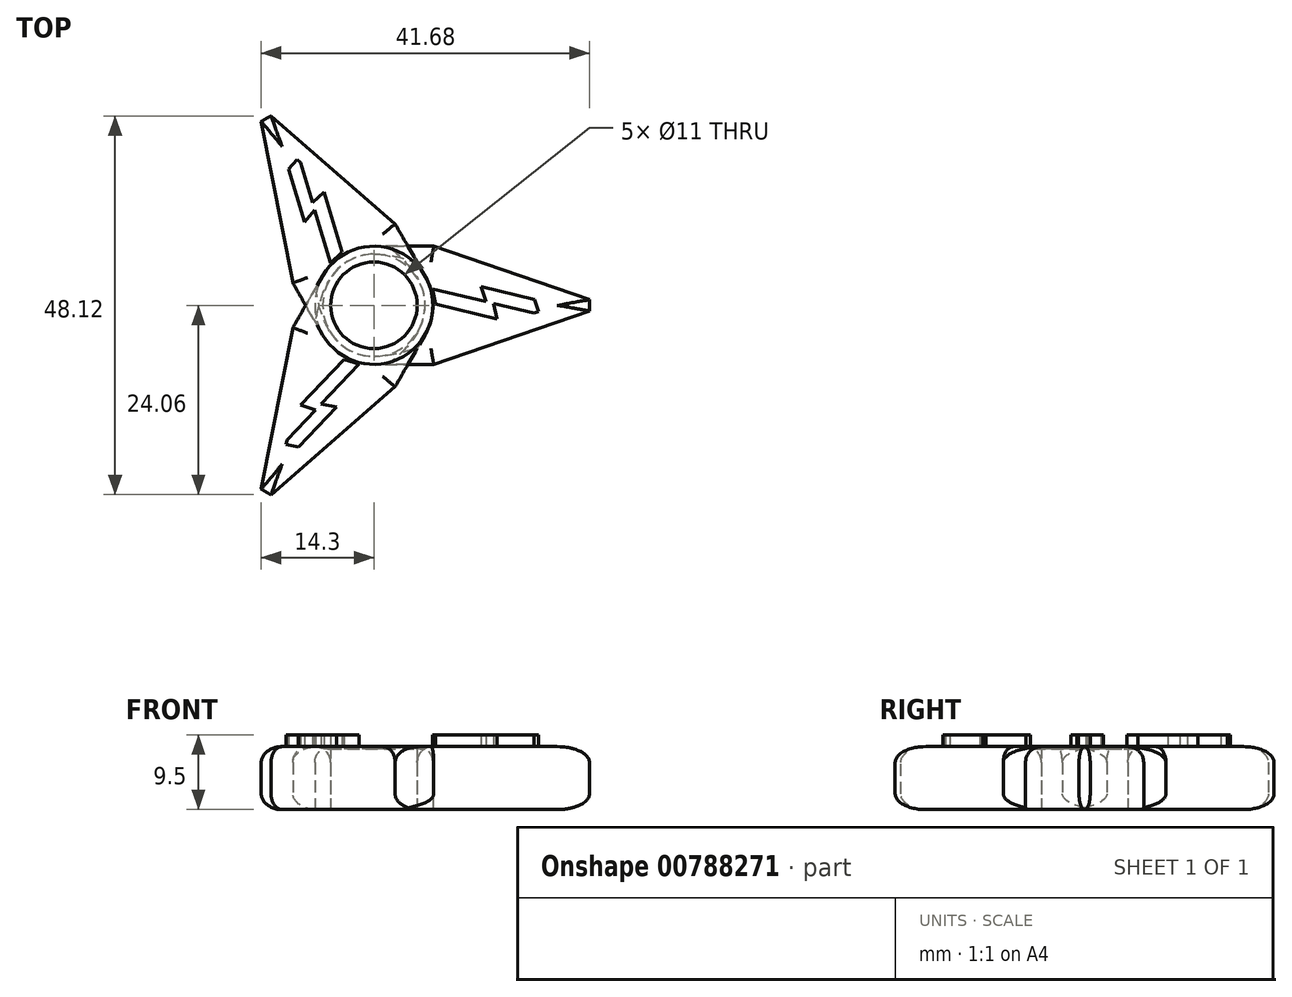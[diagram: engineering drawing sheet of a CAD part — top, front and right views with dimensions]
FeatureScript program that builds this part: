
annotation { "Feature Type Name" : "Feature", "Feature Type Description" : "" }
export const myFeature = defineFeature(function(context is Context, id is Id, definition is map)
    precondition{}
    {
        {
            var Q0;
            Q0=qCreatedBy(makeId("Top.planeOp"),FACE);
            var sketch = newSketch(context, id + "F0", { "sketchPlane" : qUnion([Q0])});
            skCircle(sketch, "E0", {"center": v(0, 0) * mm, "radius": 5.5 * mm});
            skCircle(sketch, "E1", {"center": v(0, 0) * mm, "radius": 7.5 * mm});
            skArc(sketch, "E2", {"start": v(1.87, 7.26) * mm, "mid": v(1.4, 6.35) * mm, "end": v(1, 5.4) * mm});
            skPoint(sketch, "E3.end.orphan", {"position": v(68.12, 0) * mm});
            skPoint(sketch, "E4.orphan", {"position": v(15, -15) * mm});
            skPoint(sketch, "E5.orphan", {"position": v(11.12, 14.5) * mm});
            skArc(sketch, "E6", {"start": v(13.8, 5.37) * mm, "mid": v(9.5, 0) * mm, "end": v(13.8, -5.37) * mm});
            skArc(sketch, "E7.trimOffspring", {"start": v(7.6, 13.05) * mm, "mid": v(7.49, 12.98) * mm, "end": v(7.38, 12.92) * mm});
            skPoint(sketch, "E8.end.orphan", {"position": v(69.04, 0) * mm});
            skPoint(sketch, "E9.start.orphan", {"position": v(13.6, 15) * mm});
            skPoint(sketch, "E10.start.orphan", {"position": v(0, -7.5) * mm});
            skPoint(sketch, "E11.start.orphan", {"position": v(9.16, 11) * mm});
            skPoint(sketch, "E12.start.orphan", {"position": v(0, 7.5) * mm});
            skArc(sketch, "E13", {"start": v(10.99, 6.34) * mm, "mid": v(7.5, 0) * mm, "end": v(10.99, -6.34) * mm});
            skPoint(sketch, "E14.orphan", {"position": v(13.6, 10.91) * mm});
            skPoint(sketch, "E15.orphan", {"position": v(7.5, -11.25) * mm});
            skPoint(sketch, "E16.orphan", {"position": v(5.56, 11) * mm});
            skLineSegment(sketch, "E17", {"start": v(0, 7.5) * mm, "end": v(7.6, 7.5) * mm});
            skLineSegment(sketch, "E18", {"start": v(15, 4.96) * mm, "end": v(15, -4.96) * mm});
            skLineSegment(sketch, "E19", {"start": v(7.6, -7.5) * mm, "end": v(0, -7.5) * mm});
            skLineSegment(sketch, "E20", {"start": v(0, 7.5) * mm, "end": v(0, -7.5) * mm});
            skLineSegment(sketch, "E21", {"start": v(7.6, 7.5) * mm, "end": v(29.44, 0) * mm});
            skLineSegment(sketch, "E22", {"start": v(29.44, 0) * mm, "end": v(7.6, -7.5) * mm});
            skArc(sketch, "E23.trimOffspring", {"start": v(22.06, -2.54) * mm, "mid": v(22.5, 0) * mm, "end": v(22.06, 2.54) * mm});
            skArc(sketch, "E24.trimOffspring", {"start": v(19.24, -3.5) * mm, "mid": v(20.5, 0) * mm, "end": v(19.24, 3.5) * mm});
            skSolve(sketch);
        }
        {
            var Q0;
            Q0=makeQuery(id+"F0.imprint","IMPRINT",FACE,{"disambiguationData":[TD([[makeQuery(id+"F0.imprint","IMPRINT",EDGE,{"derivedFrom":sQuery(id+"F0.wireOp",EDGE,"E0")}),-1.0]])]});
            var Q1;
            {var subQ7=sQuery(id+"F0.wireOp",EDGE,"E6");var subQ12=makeQuery(id+"F0.imprint","IMPRINT",VERTEX,{"disambiguationData":[OD(0.0)],"derivedFrom":subQ7});Q1=makeQuery(id+"F0.imprint","IMPRINT",FACE,{"disambiguationData":[TD([[makeQuery(id+"F0.imprint","IMPRINT",EDGE,{"disambiguationData":[TD([[subQ12,1.0]])],"derivedFrom":subQ7}),-1.0]])]});}
            var Q2;
            {var subQ0=sQuery(id+"F0.wireOp",EDGE,"E6");var subQ4=makeQuery(id+"F0.imprint","IMPRINT",VERTEX,{"disambiguationData":[OD(0.0)],"derivedFrom":subQ0});Q2=makeQuery(id+"F0.imprint","IMPRINT",FACE,{"disambiguationData":[TD([[makeQuery(id+"F0.imprint","IMPRINT",EDGE,{"disambiguationData":[TD([[subQ4,1.0]])],"derivedFrom":subQ0}),1.0]])]});}
            var Q3;
            {var subQ0=sQuery(id+"F0.wireOp",EDGE,"E19");Q3=makeQuery(id+"F0.imprint","IMPRINT",FACE,{"disambiguationData":[TD([[makeQuery(id+"F0.imprint","IMPRINT",EDGE,{"derivedFrom":subQ0}),-1.0]])]});}
            var Q4;
            {var subQ0=sQuery(id+"F0.wireOp",EDGE,"E17");Q4=makeQuery(id+"F0.imprint","IMPRINT",FACE,{"disambiguationData":[TD([[makeQuery(id+"F0.imprint","IMPRINT",EDGE,{"derivedFrom":subQ0}),-1.0]])]});}
            var Q5;
            {var subQ4=sQuery(id+"F0.wireOp",EDGE,"E2");Q5=makeQuery(id+"F0.imprint","IMPRINT",FACE,{"disambiguationData":[TD([[makeQuery(id+"F0.imprint","IMPRINT",EDGE,{"derivedFrom":subQ4}),1.0]])]});}
            var Q6;
            {var subQ0=sQuery(id+"F0.wireOp",EDGE,"E18");Q6=makeQuery(id+"F0.imprint","IMPRINT",FACE,{"disambiguationData":[TD([[makeQuery(id+"F0.imprint","IMPRINT",EDGE,{"derivedFrom":subQ0}),1.0]])]});}
            var Q7;
            {var subQ0=sQuery(id+"F0.wireOp",EDGE,"E23.trimOffspring");Q7=makeQuery(id+"F0.imprint","IMPRINT",FACE,{"disambiguationData":[TD([[makeQuery(id+"F0.imprint","IMPRINT",EDGE,{"derivedFrom":subQ0}),1.0]])]});}
            var Q8;
            {var subQ3=sQuery(id+"F0.wireOp",EDGE,"E23.trimOffspring");Q8=makeQuery(id+"F0.imprint","IMPRINT",FACE,{"disambiguationData":[TD([[makeQuery(id+"F0.imprint","IMPRINT",EDGE,{"derivedFrom":subQ3}),-1.0]])]});}
            extrude(context, id + "F1", {"entities" : qUnion([Q0, Q1, Q2, Q3, Q4, Q5, Q6, Q7, Q8]), "depth" : 8 * mm, "offsetDistance" : 25 * mm});
        }
        {
            var Q0;
            Q0=qCreatedBy(makeId("Right.planeOp"),FACE);
            var sketch = newSketch(context, id + "F2", { "sketchPlane" : qUnion([Q0])});
            skLineSegment(sketch, "E25", {"start": v(0, 0) * mm, "end": v(0, 45.5) * mm});
            skSolve(sketch);
        }
        {
            var Q0;
            Q0=makeQuery(id+"F1.opExtrude","SWEPT_BODY",BODY,{"disambiguationData":[OSD([sQuery(id+"F0.wireOp",EDGE,"E0"),sQuery(id+"F0.wireOp",EDGE,"E1"),sQuery(id+"F0.wireOp",EDGE,"c1pOTcFN-srbn-hujo-DCLo-aXCk1lQ58b2f"),sQuery(id+"F0.wireOp",EDGE,"E2"),sQuery(id+"F0.wireOp",EDGE,"E10"),sQuery(id+"F0.wireOp",EDGE,"E12")])]});
            var Q1;
            Q1=sQuery(id+"F2.wireOp",EDGE,"E25");
            circularPattern(context, id + "F3", {"entities" : qUnion([Q0]), "axis" : qUnion([Q1]), "angle" : 360 * degree, "instanceCount" : 3, "equalSpace" : true});
        }
        {
            var Q0;
            Q0=makeQuery(id+"F1.opExtrude","CAP_EDGE",EDGE,{"disambiguationData":[OSD([sQuery(id+"F0.wireOp",EDGE,"E22")])],"isStart":false});
            var Q1;
            Q1=makeQuery(id+"F1.opExtrude","CAP_FACE",FACE,{"disambiguationData":[OSD([sQuery(id+"F0.wireOp",EDGE,"E0"),sQuery(id+"F0.wireOp",EDGE,"E1"),sQuery(id+"F0.wireOp",EDGE,"E17"),sQuery(id+"F0.wireOp",EDGE,"E19"),sQuery(id+"F0.wireOp",EDGE,"E21"),sQuery(id+"F0.wireOp",EDGE,"E22")])],"isStart":false});
            var Q2;
            Q2=makeQuery(id+"F1.opExtrude","CAP_EDGE",EDGE,{"disambiguationData":[OSD([sQuery(id+"F0.wireOp",EDGE,"E22")])],"isStart":true});
            var Q3;
            Q3=makeQuery(id+"F1.opExtrude","CAP_EDGE",EDGE,{"disambiguationData":[OSD([sQuery(id+"F0.wireOp",EDGE,"E21")])],"isStart":true});
            var Q4;
            Q4=makeQuery(id+"F3.opPattern","COPY",EDGE,{"derivedFrom":makeQuery(id+"F1.opExtrude","CAP_EDGE",EDGE,{"disambiguationData":[OSD([sQuery(id+"F0.wireOp",EDGE,"E22")])],"isStart":true}),"instanceName":"1"});
            var Q5;
            Q5=makeQuery(id+"F3.opPattern","COPY",EDGE,{"derivedFrom":makeQuery(id+"F1.opExtrude","CAP_EDGE",EDGE,{"disambiguationData":[OSD([sQuery(id+"F0.wireOp",EDGE,"E21")])],"isStart":true}),"instanceName":"1"});
            var Q6;
            Q6=makeQuery(id+"F3.opPattern","COPY",EDGE,{"derivedFrom":makeQuery(id+"F1.opExtrude","CAP_EDGE",EDGE,{"disambiguationData":[OSD([sQuery(id+"F0.wireOp",EDGE,"E22")])],"isStart":false}),"instanceName":"1"});
            var Q7;
            Q7=makeQuery(id+"F3.opPattern","COPY",EDGE,{"derivedFrom":makeQuery(id+"F1.opExtrude","CAP_EDGE",EDGE,{"disambiguationData":[OSD([sQuery(id+"F0.wireOp",EDGE,"E21")])],"isStart":false}),"instanceName":"1"});
            var Q8;
            Q8=makeQuery(id+"F3.opPattern","COPY",EDGE,{"derivedFrom":makeQuery(id+"F1.opExtrude","CAP_EDGE",EDGE,{"disambiguationData":[OSD([sQuery(id+"F0.wireOp",EDGE,"E22")])],"isStart":false}),"instanceName":"2"});
            var Q9;
            Q9=makeQuery(id+"F3.opPattern","COPY",EDGE,{"derivedFrom":makeQuery(id+"F1.opExtrude","CAP_EDGE",EDGE,{"disambiguationData":[OSD([sQuery(id+"F0.wireOp",EDGE,"E22")])],"isStart":true}),"instanceName":"2"});
            var Q10;
            Q10=makeQuery(id+"F3.opPattern","COPY",EDGE,{"derivedFrom":makeQuery(id+"F1.opExtrude","CAP_EDGE",EDGE,{"disambiguationData":[OSD([sQuery(id+"F0.wireOp",EDGE,"E21")])],"isStart":true}),"instanceName":"2"});
            var Q11;
            Q11=makeQuery(id+"F3.opPattern","COPY",EDGE,{"derivedFrom":makeQuery(id+"F1.opExtrude","CAP_EDGE",EDGE,{"disambiguationData":[OSD([sQuery(id+"F0.wireOp",EDGE,"E21")])],"isStart":false}),"instanceName":"2"});
            fillet(context, id + "F4", {"entities" : qUnion([Q0, Q1, Q2, Q3, Q4, Q5, Q6, Q7, Q8, Q9, Q10, Q11]), "radius" : 2 * mm, "tangentPropagation" : true, "allowEdgeOverflow" : false});
        }
        {
            var Q0;
            Q0=makeQuery(id+"F1.opExtrude","SWEPT_EDGE",EDGE,{"disambiguationData":[OSD([sQuery(id+"F0.wireOp",EDGE,"E21"),sQuery(id+"F0.wireOp",EDGE,"E22")])]});
            var Q1;
            Q1=makeQuery(id+"F3.opPattern","COPY",EDGE,{"derivedFrom":makeQuery(id+"F1.opExtrude","SWEPT_EDGE",EDGE,{"disambiguationData":[OSD([sQuery(id+"F0.wireOp",EDGE,"E21"),sQuery(id+"F0.wireOp",EDGE,"E22")])]}),"instanceName":"2"});
            var Q2;
            Q2=makeQuery(id+"F3.opPattern","COPY",EDGE,{"derivedFrom":makeQuery(id+"F1.opExtrude","SWEPT_EDGE",EDGE,{"disambiguationData":[OSD([sQuery(id+"F0.wireOp",EDGE,"E21"),sQuery(id+"F0.wireOp",EDGE,"E22")])]}),"instanceName":"1"});
            chamfer(context, id + "F5", {"entities" : qUnion([Q0, Q1, Q2]), "width" : .75 * mm, "tangentPropagation" : true});
        }
        {
            var Q0;
            Q0=makeQuery(id+"F1.opExtrude","CAP_FACE",FACE,{"disambiguationData":[OSD([sQuery(id+"F0.wireOp",EDGE,"E0"),sQuery(id+"F0.wireOp",EDGE,"E1"),sQuery(id+"F0.wireOp",EDGE,"E10"),sQuery(id+"F0.wireOp",EDGE,"E12"),sQuery(id+"F0.wireOp",EDGE,"nMp6aDYQ-EUBn-gi7Y-1vA0-NtzO73nNKpQa"),sQuery(id+"F0.wireOp",EDGE,"ucYtV5Ov-8Bkq-GZmE-3TVC-n8T25JyWtEvq"),sQuery(id+"F0.wireOp",EDGE,"E11"),sQuery(id+"F0.wireOp",EDGE,"I5XwJxgH-NOVb-tVkx-Tq6v-A4jt36yrtx08"),sQuery(id+"F0.wireOp",EDGE,"dG7KTNho-NzEc-45em-pvrw-m2yzHunjuOYy"),sQuery(id+"F0.wireOp",EDGE,"ejjroDpW-kohF-Plgn-IGdK-DfK92TdWfwf9"),sQuery(id+"F0.wireOp",EDGE,"NdLykpWK-kagu-JWG3-DeJg-S52FodjAq7Sg"),sQuery(id+"F0.wireOp",EDGE,"0NwxsXWG-HWzj-xsas-FfyO-PVFYgCGhCiFI")])],"isStart":false});
            var sketch = newSketch(context, id + "F6", { "sketchPlane" : qUnion([Q0])});
            skPoint(sketch, "E26.end.orphan", {"position": v(20.02, 0) * mm});
            skPoint(sketch, "E27.orphan", {"position": v(27.12, -4.48) * mm});
            skPoint(sketch, "E28.end.orphan", {"position": v(43.2, 0) * mm});
            skPoint(sketch, "E29.end.orphan", {"position": v(27.12, -1.7) * mm});
            skLineSegment(sketch, "E30", {"start": v(7.42, 2.1) * mm, "end": v(7.86, 0.14) * mm});
            skLineSegment(sketch, "E31", {"start": v(7.86, 0.14) * mm, "end": v(15.64, -1.72) * mm});
            skLineSegment(sketch, "E32", {"start": v(15.64, -1.72) * mm, "end": v(15.2, 0.23) * mm});
            skLineSegment(sketch, "E33", {"start": v(14.23, 0.46) * mm, "end": v(7.42, 2.1) * mm});
            skLineSegment(sketch, "E34", {"start": v(15.2, 0.23) * mm, "end": v(21.03, -1.16) * mm});
            skLineSegment(sketch, "E35", {"start": v(21.03, -1.16) * mm, "end": v(20.4, 0.73) * mm});
            skLineSegment(sketch, "E36", {"start": v(20.4, 0.73) * mm, "end": v(13.58, 2.36) * mm});
            skLineSegment(sketch, "E37", {"start": v(13.58, 2.36) * mm, "end": v(14.23, 0.46) * mm});
            skPoint(sketch, "E38.end.orphan", {"position": v(8.56, -2.53) * mm});
            skPoint(sketch, "E39.orphan", {"position": v(15.66, -7) * mm});
            skPoint(sketch, "E40.end.orphan", {"position": v(31.75, -2.53) * mm});
            skPoint(sketch, "E41.end.orphan", {"position": v(15.66, -4.22) * mm});
            skSolve(sketch);
        }
        {
            var Q0;
            Q0=makeQuery(id+"F6.imprint","IMPRINT",FACE,{"disambiguationData":[TD([[makeQuery(id+"F6.imprint","IMPRINT",EDGE,{"derivedFrom":sQuery(id+"F6.wireOp",EDGE,"E26")}),1.0]])]});
            var Q1;
            {var subQ6=sQuery(id+"F6.wireOp",EDGE,"df851d8e-270d-4600-adc7-b6d222d9d4d0");Q1=makeQuery(id+"F6.imprint","IMPRINT",FACE,{"disambiguationData":[TD([[makeQuery(id+"F6.imprint","IMPRINT",EDGE,{"derivedFrom":subQ6}),1.0]])]});}
            var Q2;
            Q2=makeQuery(id+"F6.imprint","IMPRINT",FACE,{"disambiguationData":[TD([[makeQuery(id+"F6.imprint","IMPRINT",EDGE,{"derivedFrom":sQuery(id+"F6.wireOp",EDGE,"E30")}),1.0]])]});
            extrude(context, id + "F7", {"entities" : qUnion([Q0, Q1, Q2]), "operationType" : NewBodyOperationType.ADD, "depth" : 1.5 * mm, "offsetDistance" : 25 * mm});
        }
        {
            var Q0;
            Q0=makeQuery(id+"F1.opExtrude","SWEPT_BODY",BODY,{"disambiguationData":[OSD([sQuery(id+"F0.wireOp",EDGE,"E0"),sQuery(id+"F0.wireOp",EDGE,"E1"),sQuery(id+"F0.wireOp",EDGE,"E10"),sQuery(id+"F0.wireOp",EDGE,"E12"),sQuery(id+"F0.wireOp",EDGE,"nMp6aDYQ-EUBn-gi7Y-1vA0-NtzO73nNKpQa"),sQuery(id+"F0.wireOp",EDGE,"ucYtV5Ov-8Bkq-GZmE-3TVC-n8T25JyWtEvq"),sQuery(id+"F0.wireOp",EDGE,"E11"),sQuery(id+"F0.wireOp",EDGE,"I5XwJxgH-NOVb-tVkx-Tq6v-A4jt36yrtx08"),sQuery(id+"F0.wireOp",EDGE,"dG7KTNho-NzEc-45em-pvrw-m2yzHunjuOYy"),sQuery(id+"F0.wireOp",EDGE,"ejjroDpW-kohF-Plgn-IGdK-DfK92TdWfwf9"),sQuery(id+"F0.wireOp",EDGE,"NdLykpWK-kagu-JWG3-DeJg-S52FodjAq7Sg"),sQuery(id+"F0.wireOp",EDGE,"0NwxsXWG-HWzj-xsas-FfyO-PVFYgCGhCiFI")])]});
            var Q1;
            Q1=sQuery(id+"F2.wireOp",EDGE,"E25");
            circularPattern(context, id + "F8", {"entities" : qUnion([Q0]), "axis" : qUnion([Q1]), "angle" : 360 * degree, "instanceCount" : 3, "equalSpace" : true});
        }
    });
